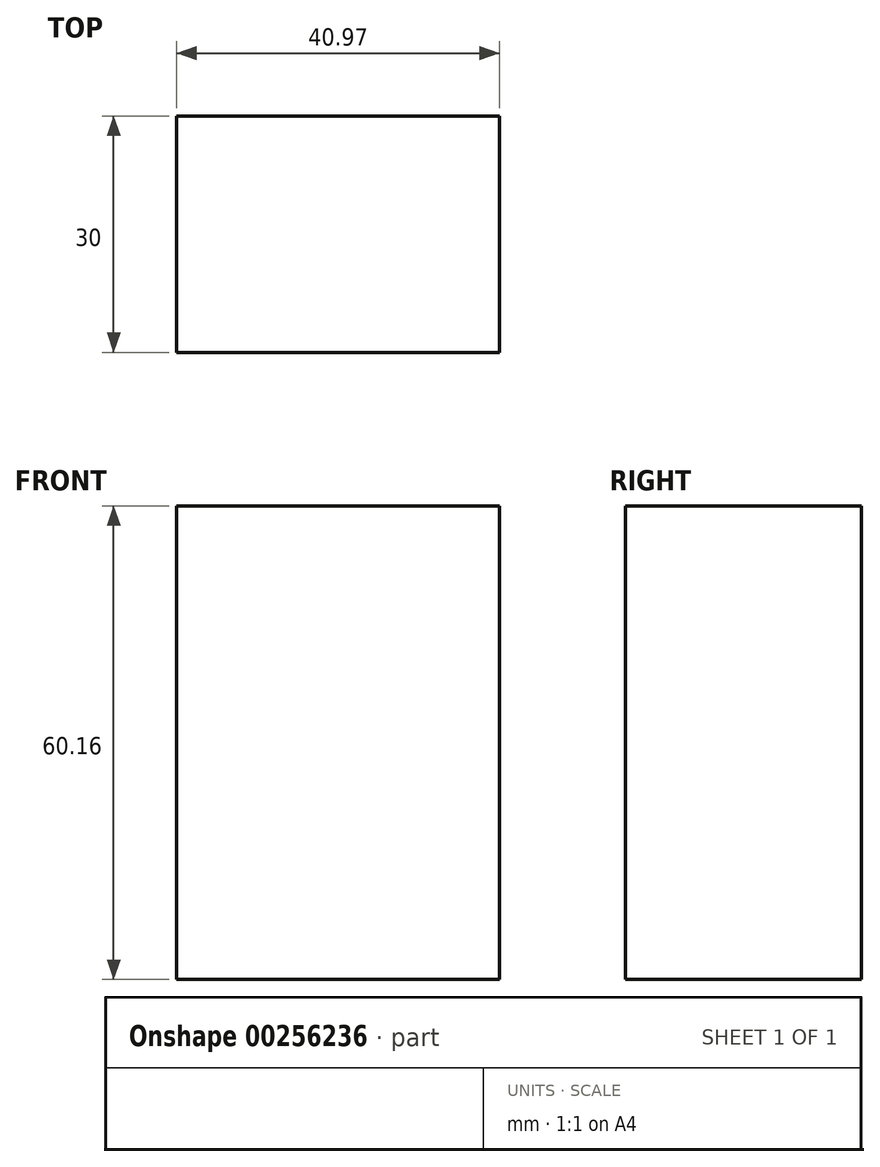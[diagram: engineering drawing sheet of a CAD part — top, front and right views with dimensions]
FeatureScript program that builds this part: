
annotation { "Feature Type Name" : "Feature", "Feature Type Description" : "" }
export const myFeature = defineFeature(function(context is Context, id is Id, definition is map)
    precondition{}
    {
        {
            var Q0;
            Q0=qCreatedBy(makeId("Front.planeOp"),FACE);
            var sketch = newSketch(context, id + "F0", { "sketchPlane" : qUnion([Q0])});
            skLineSegment(sketch, "E0.left", {"start": v(0, -12.2) * mm, "end": v(0, -12.2) * mm});
            skLineSegment(sketch, "E0.right", {"start": v(68.29, -12.2) * mm, "end": v(68.29, -12.2) * mm});
            skLineSegment(sketch, "E1.bottom", {"start": v(57.83, -12.5) * mm, "end": v(57.83, -12.5) * mm});
            skLineSegment(sketch, "E1.top", {"start": v(57.83, -12.5) * mm, "end": v(57.83, -12.5) * mm});
            skLineSegment(sketch, "E1.left", {"start": v(57.83, -12.5) * mm, "end": v(57.83, -12.5) * mm});
            skLineSegment(sketch, "E1.right", {"start": v(57.83, -12.5) * mm, "end": v(57.83, -12.5) * mm});
            skLineSegment(sketch, "E2.left", {"start": v(57.83, -12.5) * mm, "end": v(57.83, -12.79) * mm});
            skLineSegment(sketch, "E2.right", {"start": v(68.29, -12.5) * mm, "end": v(68.29, -12.79) * mm});
            skLineSegment(sketch, "E3.right", {"start": v(33.42, -12.5) * mm, "end": v(33.7, -12.5) * mm});
            skLineSegment(sketch, "E4.left", {"start": v(33.7, -12.5) * mm, "end": v(33.7, -12.5) * mm});
            skLineSegment(sketch, "E5.bottom", {"start": v(68.29, -12.5) * mm, "end": v(68.29, -12.5) * mm});
            skLineSegment(sketch, "E5.top", {"start": v(68.29, -12.5) * mm, "end": v(68.29, -12.5) * mm});
            skLineSegment(sketch, "E5.left", {"start": v(68.29, -12.5) * mm, "end": v(68.29, -12.5) * mm});
            skLineSegment(sketch, "E5.right", {"start": v(68.29, -12.5) * mm, "end": v(68.29, -12.5) * mm});
            skLineSegment(sketch, "E6.bottom", {"start": v(34, -38.36) * mm, "end": v(34, -38.36) * mm});
            skLineSegment(sketch, "E6.top", {"start": v(34, -38.36) * mm, "end": v(34, -38.36) * mm});
            skLineSegment(sketch, "E6.left", {"start": v(34, -38.36) * mm, "end": v(34, -38.36) * mm});
            skLineSegment(sketch, "E6.right", {"start": v(34, -38.36) * mm, "end": v(34, -38.36) * mm});
            skLineSegment(sketch, "E7.bottom", {"start": v(0, -2.32) * mm, "end": v(40.97, -2.32) * mm});
            skLineSegment(sketch, "E7.top", {"start": v(0, -62.48) * mm, "end": v(40.97, -62.48) * mm});
            skLineSegment(sketch, "E7.left", {"start": v(0, -2.32) * mm, "end": v(0, -62.48) * mm});
            skLineSegment(sketch, "E7.right", {"start": v(40.97, -2.32) * mm, "end": v(40.97, -62.48) * mm});
            skLineSegment(sketch, "E8.bottom", {"start": v(-101.42, -36.32) * mm, "end": v(-101.42, -36.32) * mm});
            skLineSegment(sketch, "E8.top", {"start": v(-101.42, -5.52) * mm, "end": v(-101.42, -5.52) * mm});
            skLineSegment(sketch, "E8.left", {"start": v(-101.42, -36.32) * mm, "end": v(-101.42, -5.52) * mm});
            skSolve(sketch);
        }
        {
            var Q0;
            Q0=makeQuery(id+"F0.imprint","IMPRINT",FACE,{"disambiguationData":[TD([[makeQuery(id+"F0.imprint","IMPRINT",EDGE,{"derivedFrom":sQuery(id+"F0.wireOp",EDGE,"E7.bottom")}),-1.0]])]});
            extrude(context, id + "F1", {"entities" : qUnion([Q0]), "depth" : 30 * mm});
        }
    });
